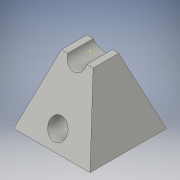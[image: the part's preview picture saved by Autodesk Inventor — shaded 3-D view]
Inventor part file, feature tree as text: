
AUTODESK INVENTOR PART (.ipt)
format: ipt  version: 2016 SP1 (Build 200210100, 210)  size: 118,784 bytes
history: native  units: in
note: dims shown in document units (in); Inventor stores cm internally (conversion verified against a paired STEP export)
features: sketch x4, plane x2, other x1, loft x1, extrude x1
ambient origin geometry x8: Origin, YZ Plane, XZ Plane, XY Plane, X Axis, Y Axis, Z Axis, Center Point
bodies: Solid1 (feature_tree)
feature tree (9):
  parser-record x1  (decoder bookkeeping rows leaked as tree rows — omitted from the tree; the rows remain in map.json)
  sketch  "Sketch2"  dims[d2=1.5in d3=1.5in]
  plane  "Work Plane1"
  sketch  "Sketch3"  dims[d4=1.3125in d5=0.625in]
  loft  "Loft1"
  plane  "Work Plane2"
  extrude  "Extrusion2"  Depth=1.3125in
  sketch  "Sketch6"  dims[d11=0.0in d12=90.0deg d13=0.0in d14=90.0deg d17=0.375in d19=0.3125in d20=0.375in d21=1.0in d22=1.0in d23=0.0in]
  sketch  "Sketch5"  dims[d6=0.5in]
note: 1 file-system path scrubbed to <path> (originals preserved in map.json)
